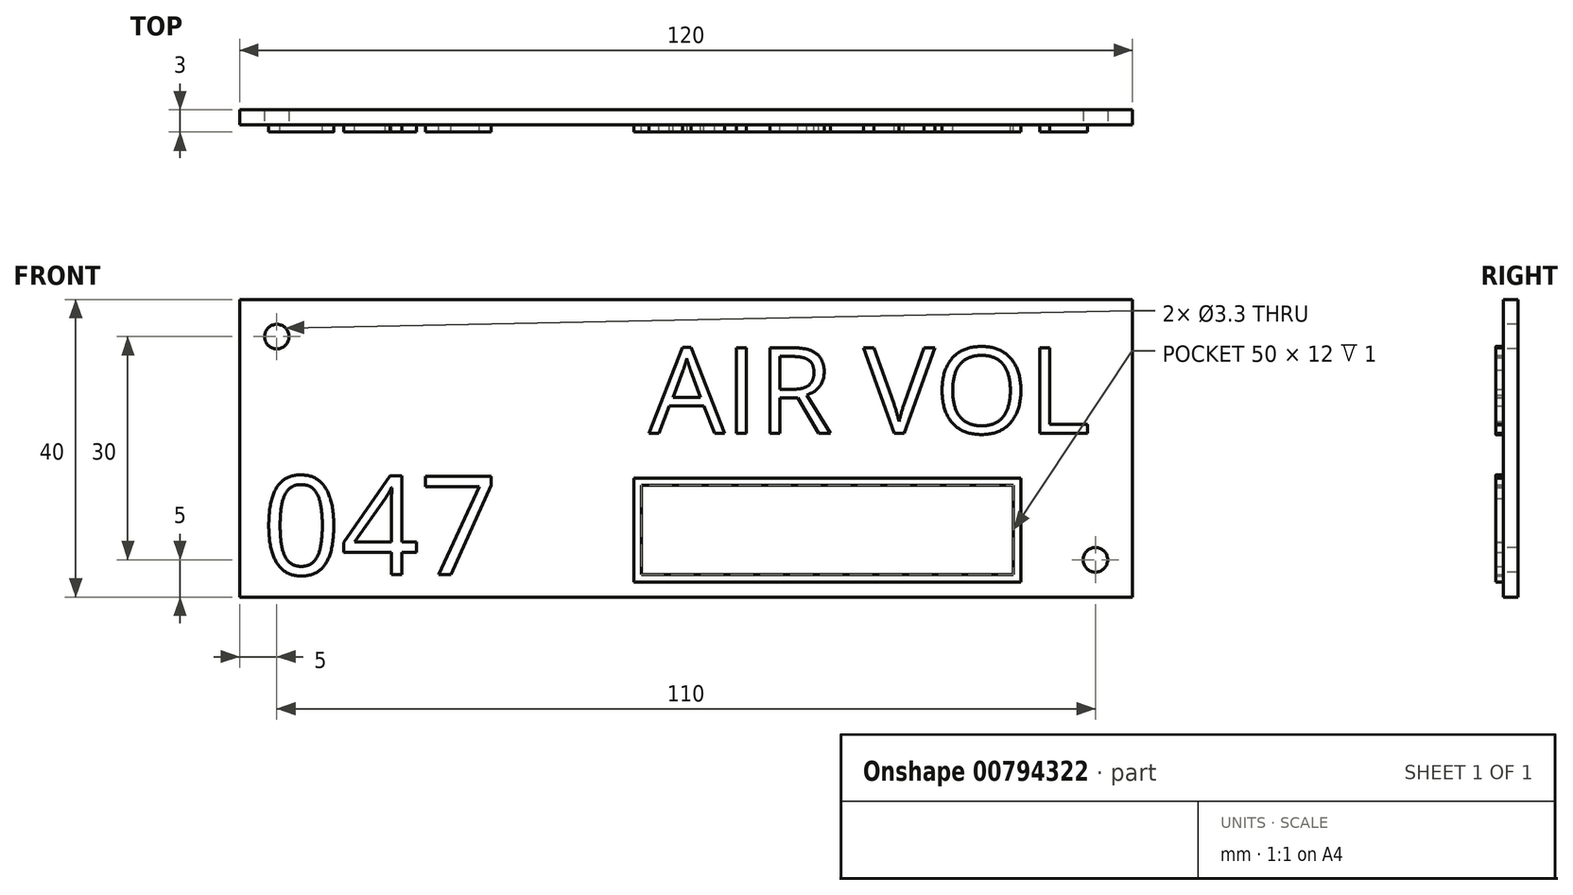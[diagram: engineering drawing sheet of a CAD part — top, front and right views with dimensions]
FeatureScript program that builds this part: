
annotation { "Feature Type Name" : "Feature", "Feature Type Description" : "" }
export const myFeature = defineFeature(function(context is Context, id is Id, definition is map)
    precondition{}
    {
        {
            var Q0;
            Q0=qCreatedBy(makeId("Front.planeOp"),FACE);
            var sketch = newSketch(context, id + "F0", { "sketchPlane" : qUnion([Q0])});
            skLineSegment(sketch, "E0.bottom", {"start": v(60, -20) * mm, "end": v(-60, -20) * mm});
            skLineSegment(sketch, "E0.top", {"start": v(60, 20) * mm, "end": v(-60, 20) * mm});
            skLineSegment(sketch, "E0.left", {"start": v(60, -20) * mm, "end": v(60, 20) * mm});
            skLineSegment(sketch, "E0.right", {"start": v(-60, -20) * mm, "end": v(-60, 20) * mm});
            skPoint(sketch, "E0.middle", {"position": v(0, 0) * mm});
            skSolve(sketch);
        }
        {
            var Q0;
            Q0=makeQuery(id+"F0.imprint","IMPRINT",FACE,{"disambiguationData":[TD([[makeQuery(id+"F0.imprint","IMPRINT",EDGE,{"derivedFrom":sQuery(id+"F0.wireOp",EDGE,"E0.bottom")}),-1.0]])]});
            extrude(context, id + "F1", {"entities" : qUnion([Q0]), "depth" : 2 * mm});
        }
        {
            var Q0;
            Q0=makeQuery(id+"F1.opExtrude","CAP_FACE",FACE,{"disambiguationData":[OSD([sQuery(id+"F0.wireOp",EDGE,"E0.bottom"),sQuery(id+"F0.wireOp",EDGE,"E0.top"),sQuery(id+"F0.wireOp",EDGE,"E0.left"),sQuery(id+"F0.wireOp",EDGE,"E0.right")])],"isStart":false});
            var sketch = newSketch(context, id + "F2", { "sketchPlane" : qUnion([Q0])});
            skPoint(sketch, "E1", {"position": v(-55, 15) * mm});
            skPoint(sketch, "E2", {"position": v(55, -15) * mm});
            skSolve(sketch);
        }
        {
            var Q0;
            Q0=sQuery(id+"F2.wireOp",VERTEX,"E1");
            var Q1;
            Q1=sQuery(id+"F2.wireOp",VERTEX,"E2");
            var Q2;
            Q2=makeQuery(id+"F1.opExtrude","SWEPT_BODY",BODY,{"disambiguationData":[OSD([sQuery(id+"F0.wireOp",EDGE,"E0.bottom"),sQuery(id+"F0.wireOp",EDGE,"E0.top"),sQuery(id+"F0.wireOp",EDGE,"E0.left"),sQuery(id+"F0.wireOp",EDGE,"E0.right")])]});
            hole(context, id + "F3", {"style" : HoleStyle.SIMPLE, "endStyle" : HoleEndStyle.THROUGH, "holeDiameter" : 3.3 * mm, "locations" : qUnion([Q0, Q1]), "scope" : qUnion([Q2]), "isTappedThrough" : true});
        }
        {
            var Q0;
            Q0=makeQuery(id+"F1.opExtrude","CAP_FACE",FACE,{"disambiguationData":[OSD([sQuery(id+"F0.wireOp",EDGE,"E0.bottom"),sQuery(id+"F0.wireOp",EDGE,"E0.top"),sQuery(id+"F0.wireOp",EDGE,"E0.left"),sQuery(id+"F0.wireOp",EDGE,"E0.right")])],"isStart":false});
            var sketch = newSketch(context, id + "F4", { "sketchPlane" : qUnion([Q0])});
            skText(sketch, "E3", { "text": "AIR VOL", "fontName": "OpenSans-Regular.ttf"});
            const initialGuessF4  = {"E3": [-0.005, 0.002, 1, 0, 0.0116]};
            skSetInitialGuess(sketch, initialGuessF4);
            skSolve(sketch);
        }
        {
            var Q0;
            Q0=qSketchRegion(id+"F4",true);
            extrude(context, id + "F5", {"entities" : qUnion([Q0]), "operationType" : NewBodyOperationType.ADD, "depth" : 1 * mm});
        }
        {
            var Q0;
            {var subQ0=sQuery(id+"F0.wireOp",EDGE,"E0.top");var subQ1=sQuery(id+"F0.wireOp",EDGE,"E0.left");var subQ2=sQuery(id+"F0.wireOp",EDGE,"E0.right");var subQ3=sQuery(id+"F0.wireOp",EDGE,"E0.bottom");Q0=makeQuery(id+"F5.boolean.opBoolean","SPLIT",FACE,{"disambiguationData":[TD([makeQuery(id+"F1.opExtrude","SWEPT_FACE",FACE,{"disambiguationData":[OSD([subQ3])]})])],"derivedFrom":makeQuery(id+"F1.opExtrude","CAP_FACE",FACE,{"disambiguationData":[OSD([subQ3,subQ0,subQ1,subQ2])],"isStart":false})});}
            var sketch = newSketch(context, id + "F6", { "sketchPlane" : qUnion([Q0])});
            skText(sketch, "E4", { "text": "047", "fontName": "OpenSans-Regular.ttf"});
            const initialGuessF6  = {"E4": [-0.057, -0.017, 1, 0, 0.01332]};
            skSetInitialGuess(sketch, initialGuessF6);
            skSolve(sketch);
        }
        {
            var Q0;
            Q0=qSketchRegion(id+"F6",true);
            extrude(context, id + "F7", {"entities" : qUnion([Q0]), "operationType" : NewBodyOperationType.ADD, "depth" : 1 * mm});
        }
        {
            var Q0;
            {var subQ46=sQuery(id+"F0.wireOp",EDGE,"E0.top");var subQ48=sQuery(id+"F0.wireOp",EDGE,"E0.left");var subQ66=sQuery(id+"F0.wireOp",EDGE,"E0.right");var subQ76=sQuery(id+"F0.wireOp",EDGE,"E0.bottom");var subQ77=makeQuery(id+"F1.opExtrude","SWEPT_FACE",FACE,{"disambiguationData":[OSD([subQ76])]});Q0=makeQuery(id+"F7.boolean.opBoolean","SPLIT",FACE,{"disambiguationData":[TD([subQ77])],"derivedFrom":makeQuery(id+"F5.boolean.opBoolean","SPLIT",FACE,{"disambiguationData":[TD([subQ77])],"derivedFrom":makeQuery(id+"F1.opExtrude","CAP_FACE",FACE,{"disambiguationData":[OSD([subQ76,subQ46,subQ48,subQ66])],"isStart":false})})});}
            var sketch = newSketch(context, id + "F8", { "sketchPlane" : qUnion([Q0])});
            skLineSegment(sketch, "E5.bottom", {"start": v(45, -18) * mm, "end": v(-7, -18) * mm});
            skLineSegment(sketch, "E5.top", {"start": v(45, -4) * mm, "end": v(-7, -4) * mm});
            skLineSegment(sketch, "E5.left", {"start": v(45, -18) * mm, "end": v(45, -4) * mm});
            skLineSegment(sketch, "E5.right", {"start": v(-7, -18) * mm, "end": v(-7, -4) * mm});
            skPoint(sketch, "E5.middle", {"position": v(19, -11) * mm});
            skLineSegment(sketch, "E6.0", {"start": v(44, -5) * mm, "end": v(-6, -5) * mm});
            skLineSegment(sketch, "E6.1", {"start": v(44, -17) * mm, "end": v(44, -5) * mm});
            skLineSegment(sketch, "E6.2", {"start": v(44, -17) * mm, "end": v(-6, -17) * mm});
            skLineSegment(sketch, "E6.3", {"start": v(-6, -17) * mm, "end": v(-6, -5) * mm});
            skSolve(sketch);
        }
        {
            var Q0;
            Q0=makeQuery(id+"F8.imprint","IMPRINT",FACE,{"disambiguationData":[TD([[makeQuery(id+"F8.imprint","IMPRINT",EDGE,{"derivedFrom":sQuery(id+"F8.wireOp",EDGE,"E5.bottom")}),-1.0]])]});
            extrude(context, id + "F9", {"entities" : qUnion([Q0]), "operationType" : NewBodyOperationType.ADD, "depth" : 1 * mm});
        }
    });
